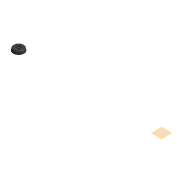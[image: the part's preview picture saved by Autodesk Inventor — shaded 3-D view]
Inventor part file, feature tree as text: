
AUTODESK INVENTOR PART (.ipt)
format: ipt  version: 2014 (Build 180170000, 170)  size: 117,248 bytes
history: native  units: mm
features: extrude x4, sketch x4, reference x3, plane x1, fillet x1
ambient origin geometry x8: Origin, YZ Plane, XZ Plane, XY Plane, X Axis, Y Axis, Z Axis, Center Point
bodies: Solid1 (feature_tree)
feature tree (13):
  plane  "Work Plane1"
  extrude  "Extrusion1"  Depth=23.0mm
  fillet  "Fillet1"  Radius=23.0mm
  extrude  "Extrusion2"  Depth=2.0mm
  extrude  "Extrusion3"  Depth=3.0mm TaperAngle=0.0deg
  extrude  "Extrusion4"  Depth=3.0mm TaperAngle=0.0deg
  sketch  "Sketch1"  dims[d0=23.0mm d1=23.0mm d2=23.0mm]
  reference  "Reference1"
  reference  "Reference2"
  reference  "Reference3"
  sketch  "Sketch2"  dims[d3=6.0mm d4=-1.745329mm d5=2.0mm]
  sketch  "Sketch3"  dims[d6=10.0mm d7=3.0mm d8=0.0mm]
  sketch  "Sketch4"  dims[d9=4.0mm d10=3.0mm d11=0.0mm d12=16.0mm d13=0.5mm d14=0.0mm]
